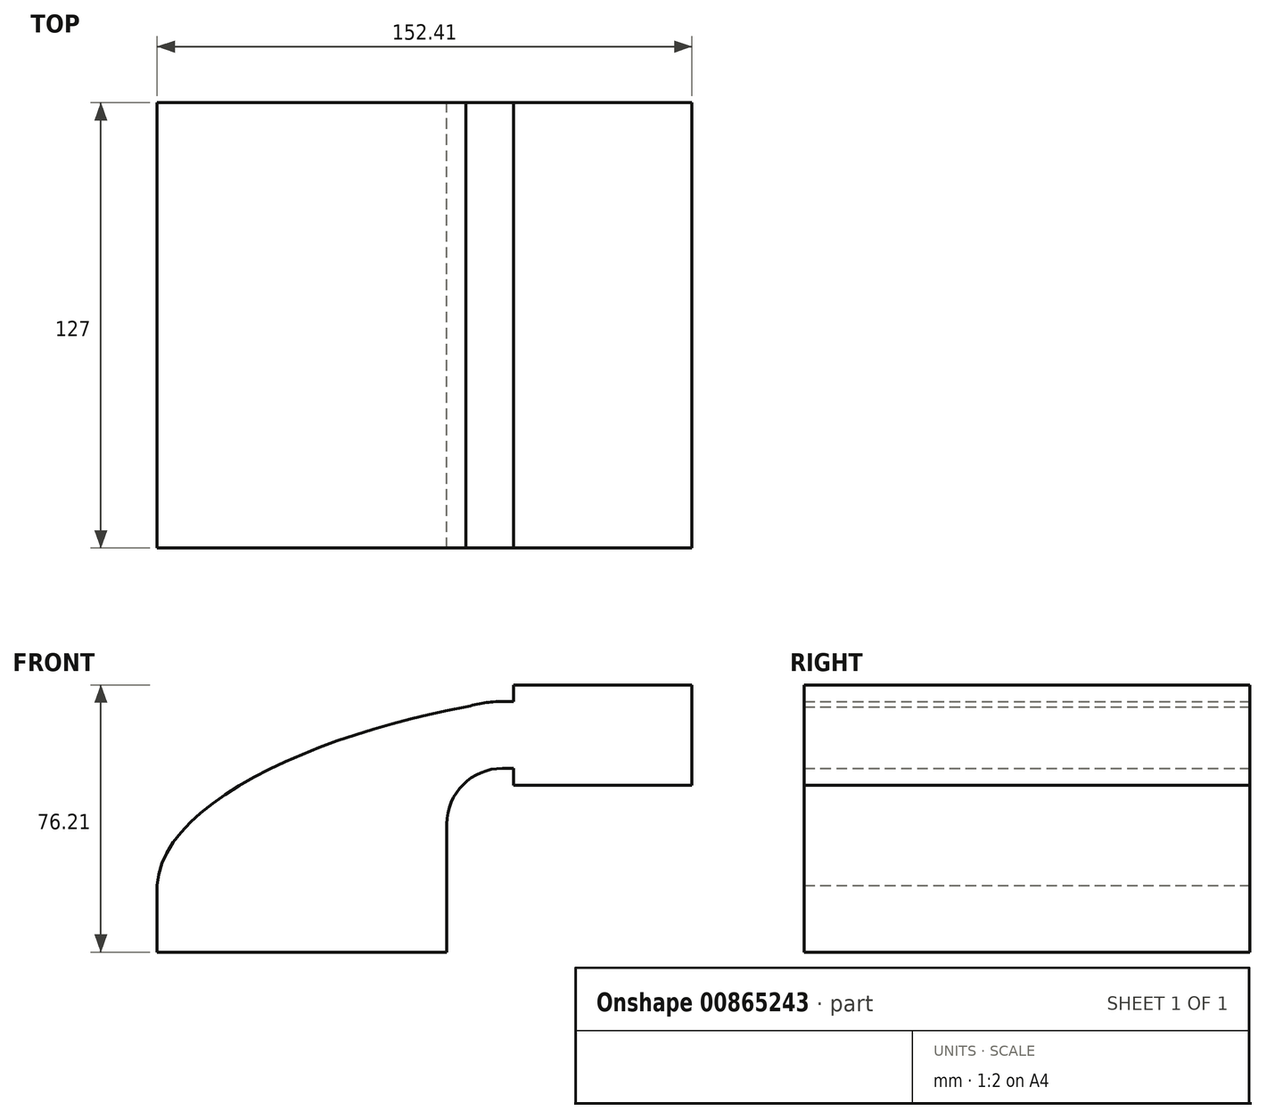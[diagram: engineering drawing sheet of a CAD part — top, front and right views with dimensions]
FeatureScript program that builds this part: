
annotation { "Feature Type Name" : "Feature", "Feature Type Description" : "" }
export const myFeature = defineFeature(function(context is Context, id is Id, definition is map)
    precondition{}
    {
        {
            var Q0;
            Q0=qCreatedBy(makeId("Front.planeOp"),FACE);
            var sketch = newSketch(context, id + "F0", { "sketchPlane" : qUnion([Q0])});
            skLineSegment(sketch, "E0.bottom", {"start": v(-41.28, -9.53) * mm, "end": v(41.28, -9.53) * mm});
            skLineSegment(sketch, "E0.top", {"start": v(-41.28, 9.53) * mm, "end": v(41.28, 9.53) * mm});
            skLineSegment(sketch, "E0.left", {"start": v(-41.28, -9.53) * mm, "end": v(-41.28, 9.53) * mm});
            skLineSegment(sketch, "E0.right", {"start": v(41.28, -9.53) * mm, "end": v(41.28, 9.53) * mm});
            skPoint(sketch, "E0.middle", {"position": v(0, 0) * mm});
            skLineSegment(sketch, "E1.bottom", {"start": v(111.12, 38.1) * mm, "end": v(60.33, 38.1) * mm});
            skLineSegment(sketch, "E1.top", {"start": v(111.12, 66.68) * mm, "end": v(60.33, 66.68) * mm});
            skLineSegment(sketch, "E1.left", {"start": v(111.12, 38.1) * mm, "end": v(111.12, 66.68) * mm});
            skLineSegment(sketch, "E1.right", {"start": v(60.33, 38.1) * mm, "end": v(60.33, 66.68) * mm});
            skPoint(sketch, "E1.middle", {"position": v(85.72, 52.39) * mm});
            skLineSegment(sketch, "E2", {"start": v(41.28, 9.53) * mm, "end": v(41.28, 27) * mm});
            skArc(sketch, "E3", {"start": v(41.27, 27) * mm, "mid": v(45.92, 38.23) * mm, "end": v(57.15, 42.88) * mm});
            skLineSegment(sketch, "E4", {"start": v(57.15, 42.88) * mm, "end": v(85.5, 42.88) * mm});
            skLineSegment(sketch, "E5.0", {"start": v(57.15, 61.93) * mm, "end": v(85.72, 61.93) * mm});
            skArc(sketch, "E5.1", {"start": v(22.23, 27) * mm, "mid": v(32.45, 51.7) * mm, "end": v(57.15, 61.93) * mm});
            skLineSegment(sketch, "E5.2", {"start": v(22.22, 9.53) * mm, "end": v(22.22, 27) * mm});
            skLineSegment(sketch, "E6", {"start": v(85.72, 38.1) * mm, "end": v(85.72, 66.68) * mm});
            skFitSpline(sketch, "E7", {"points": [v(-41.28, 9.53) * mm, v(57.15, 61.93) * mm], "startDerivative": vector(4.53, 79.7) * mm, "endDerivative": vector(123.4, 15.54) * mm});
            skSolve(sketch);
        }
        {
            var Q0;
            Q0 = qSketchRegion(id + "F0", true);
            extrude(context, id + "F1", {"entities" : qUnion([Q0]), "endBound" : BoundingType.SYMMETRIC, "depth" : 127 * mm, "offsetDistance" : 25.4 * mm});
        }
    });
